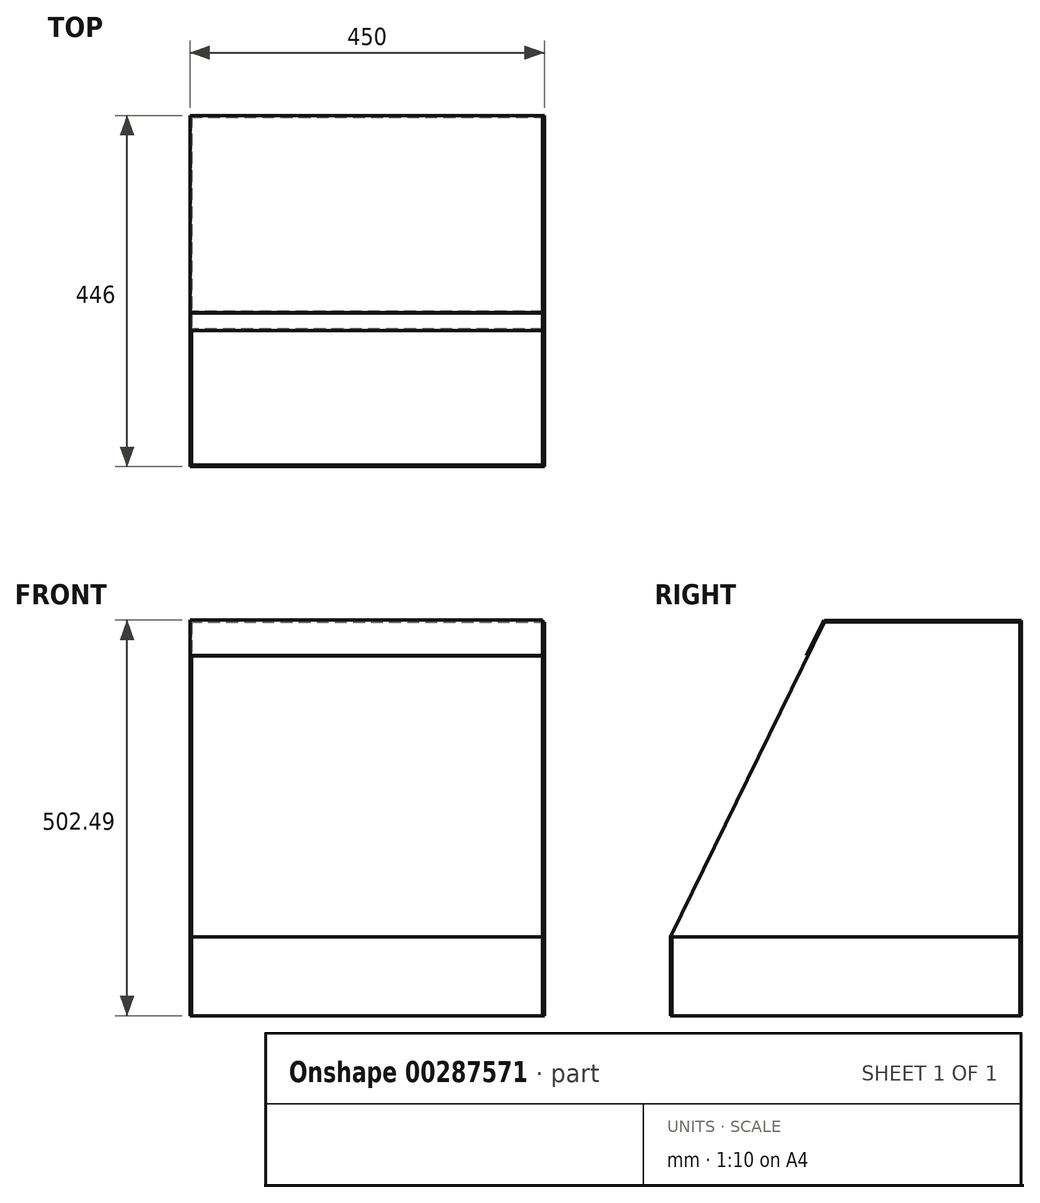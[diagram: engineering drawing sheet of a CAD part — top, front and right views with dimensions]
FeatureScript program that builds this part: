
annotation { "Feature Type Name" : "Feature", "Feature Type Description" : "" }
export const myFeature = defineFeature(function(context is Context, id is Id, definition is map)
    precondition{}
    {
        {
            var Q0;
            Q0=qCreatedBy(makeId("Top.planeOp"),FACE);
            var sketch = newSketch(context, id + "F0", { "sketchPlane" : qUnion([Q0])});
            skLineSegment(sketch, "E0.bottom", {"start": v(0, 448) * mm, "end": v(2, 448) * mm});
            skLineSegment(sketch, "E0.top", {"start": v(0, 2) * mm, "end": v(2, 2) * mm});
            skLineSegment(sketch, "E0.left", {"start": v(0, 448) * mm, "end": v(0, 2) * mm});
            skLineSegment(sketch, "E0.right", {"start": v(2, 448) * mm, "end": v(2, 2) * mm});
            skLineSegment(sketch, "E1.bottom", {"start": v(448, 448) * mm, "end": v(450, 448) * mm});
            skLineSegment(sketch, "E1.top", {"start": v(448, 2) * mm, "end": v(450, 2) * mm});
            skLineSegment(sketch, "E1.left", {"start": v(448, 448) * mm, "end": v(448, 2) * mm});
            skLineSegment(sketch, "E1.right", {"start": v(450, 448) * mm, "end": v(450, 2) * mm});
            skLineSegment(sketch, "E2.bottom", {"start": v(0, 450) * mm, "end": v(450, 450) * mm});
            skLineSegment(sketch, "E2.top", {"start": v(0, 448) * mm, "end": v(450, 448) * mm});
            skLineSegment(sketch, "E2.left", {"start": v(0, 450) * mm, "end": v(0, 448) * mm});
            skLineSegment(sketch, "E2.right", {"start": v(450, 450) * mm, "end": v(450, 448) * mm});
            skLineSegment(sketch, "E3.bottom", {"start": v(0, 2) * mm, "end": v(450, 2) * mm});
            skLineSegment(sketch, "E3.top", {"start": v(0, 0) * mm, "end": v(450, 0) * mm});
            skLineSegment(sketch, "E3.left", {"start": v(0, 2) * mm, "end": v(0, 0) * mm});
            skLineSegment(sketch, "E3.right", {"start": v(450, 2) * mm, "end": v(450, 0) * mm});
            skSolve(sketch);
        }
        {
            var Q0;
            Q0=sQuery(id+"F0.wireOp",EDGE,"E0.left");
            var Q1;
            Q1=sQuery(id+"F0.wireOp",EDGE,"E3.bottom");
            var Q2;
            Q2=sQuery(id+"F0.wireOp",EDGE,"E1.right");
            var Q3;
            Q3=sQuery(id+"F0.wireOp",EDGE,"E2.top");
            extrude(context, id + "F1", {"bodyType" : ToolBodyType.SURFACE, "surfaceEntities" : qUnion([Q0, Q1, Q2, Q3]), "depth" : 100 * mm});
        }
        {
            var Q0;
            Q0=makeQuery(id+"F1.opExtrude","SWEPT_FACE",FACE,{"disambiguationData":[OSD([sQuery(id+"F0.wireOp",EDGE,"E1.right")])]});
            var sketch = newSketch(context, id + "F2", { "sketchPlane" : qUnion([Q0])});
            skLineSegment(sketch, "E4", {"start": v(2, 100) * mm, "end": v(198, 500) * mm});
            skLineSegment(sketch, "E5", {"start": v(198, 500) * mm, "end": v(448, 500) * mm});
            skLineSegment(sketch, "E6", {"start": v(448, 500) * mm, "end": v(448, 100) * mm});
            skLineSegment(sketch, "E7", {"start": v(448, 100) * mm, "end": v(2, 100) * mm});
            skSolve(sketch);
        }
        {
            var Q0;
            Q0=makeQuery(id+"F2.imprint","IMPRINT",FACE,{"disambiguationData":[TD([[makeQuery(id+"F2.imprint","IMPRINT",EDGE,{"derivedFrom":sQuery(id+"F2.wireOp",EDGE,"E4")}),-1.0]])]});
            extrude(context, id + "F3", {"entities" : qUnion([Q0]), "oppositeDirection" : true, "depth" : 2 * mm});
        }
        {
            var Q0;
            Q0=makeQuery(id+"F1.opExtrude","SWEPT_FACE",FACE,{"disambiguationData":[OSD([sQuery(id+"F0.wireOp",EDGE,"E0.left")])]});
            var sketch = newSketch(context, id + "F4", { "sketchPlane" : qUnion([Q0])});
            skLineSegment(sketch, "E8", {"start": v(-2, 100) * mm, "end": v(-198, 500) * mm});
            skLineSegment(sketch, "E9", {"start": v(-198, 500) * mm, "end": v(-448, 500) * mm});
            skLineSegment(sketch, "E10", {"start": v(-448, 500) * mm, "end": v(-448, 100) * mm});
            skLineSegment(sketch, "E11", {"start": v(-448, 100) * mm, "end": v(-2, 100) * mm});
            skSolve(sketch);
        }
        {
            var Q0;
            Q0=makeQuery(id+"F4.imprint","IMPRINT",FACE,{"disambiguationData":[TD([[makeQuery(id+"F4.imprint","IMPRINT",EDGE,{"derivedFrom":sQuery(id+"F4.wireOp",EDGE,"E8")}),1.0]])]});
            extrude(context, id + "F5", {"entities" : qUnion([Q0]), "oppositeDirection" : true, "depth" : 2 * mm});
        }
        {
            var Q0;
            Q0=makeQuery(id+"F1.opExtrude","SWEPT_FACE",FACE,{"disambiguationData":[OSD([sQuery(id+"F0.wireOp",EDGE,"E2.top")])]});
            var sketch = newSketch(context, id + "F6", { "sketchPlane" : qUnion([Q0])});
            skLineSegment(sketch, "E12", {"start": v(-450, 100) * mm, "end": v(0, 100) * mm});
            skLineSegment(sketch, "E13", {"start": v(0, 100) * mm, "end": v(0, 500) * mm});
            skLineSegment(sketch, "E14", {"start": v(0, 500) * mm, "end": v(-450, 500) * mm});
            skLineSegment(sketch, "E15", {"start": v(-450, 500) * mm, "end": v(-450, 100) * mm});
            skSolve(sketch);
        }
        {
            var Q0;
            Q0=makeQuery(id+"F6.imprint","IMPRINT",FACE,{"disambiguationData":[TD([[makeQuery(id+"F6.imprint","IMPRINT",EDGE,{"derivedFrom":sQuery(id+"F6.wireOp",EDGE,"E12")}),1.0]])]});
            extrude(context, id + "F7", {"entities" : qUnion([Q0]), "oppositeDirection" : true, "depth" : 2 * mm});
        }
        {
            var Q0;
            Q0=makeQuery(id+"F3.opExtrude","SWEPT_FACE",FACE,{"disambiguationData":[OSD([sQuery(id+"F2.wireOp",EDGE,"E5")])]});
            var sketch = newSketch(context, id + "F8", { "sketchPlane" : qUnion([Q0])});
            skLineSegment(sketch, "E16.bottom", {"start": v(0, 448) * mm, "end": v(450, 448) * mm});
            skLineSegment(sketch, "E16.top", {"start": v(0, 198) * mm, "end": v(450, 198) * mm});
            skLineSegment(sketch, "E16.left", {"start": v(0, 448) * mm, "end": v(0, 198) * mm});
            skLineSegment(sketch, "E16.right", {"start": v(450, 448) * mm, "end": v(450, 198) * mm});
            skSolve(sketch);
        }
        {
            var Q0;
            {var subQ2=sQuery(id+"F8.wireOp",EDGE,"E16.left");Q0=makeQuery(id+"F8.imprint","IMPRINT",FACE,{"disambiguationData":[TD([[makeQuery(id+"F8.imprint","IMPRINT",EDGE,{"derivedFrom":subQ2}),1.0]])]});}
            extrude(context, id + "F9", {"entities" : qUnion([Q0]), "depth" : 2 * mm});
        }
        {
            var Q0;
            Q0=makeQuery(id+"F1.opExtrude","SWEPT_FACE",FACE,{"disambiguationData":[OSD([sQuery(id+"F0.wireOp",EDGE,"E2.top")])]});
            extrude(context, id + "F10", {"entities" : qUnion([Q0]), "oppositeDirection" : true, "depth" : 2 * mm});
        }
        {
            var Q0;
            Q0=makeQuery(id+"F1.opExtrude","SWEPT_FACE",FACE,{"disambiguationData":[OSD([sQuery(id+"F0.wireOp",EDGE,"E0.left")])]});
            extrude(context, id + "F11", {"entities" : qUnion([Q0]), "oppositeDirection" : true, "depth" : 2 * mm});
        }
        {
            var Q0;
            Q0=makeQuery(id+"F1.opExtrude","SWEPT_FACE",FACE,{"disambiguationData":[OSD([sQuery(id+"F0.wireOp",EDGE,"E3.bottom")])]});
            extrude(context, id + "F12", {"entities" : qUnion([Q0]), "oppositeDirection" : true, "depth" : 2 * mm});
        }
        {
            var Q0;
            Q0=makeQuery(id+"F1.opExtrude","SWEPT_FACE",FACE,{"disambiguationData":[OSD([sQuery(id+"F0.wireOp",EDGE,"E1.right")])]});
            extrude(context, id + "F13", {"entities" : qUnion([Q0]), "oppositeDirection" : true, "depth" : 2 * mm});
        }
        {
            var Q0;
            Q0=makeQuery(id+"F3.opExtrude","SWEPT_FACE",FACE,{"disambiguationData":[OSD([sQuery(id+"F2.wireOp",EDGE,"E4")])]});
            var sketch = newSketch(context, id + "F14", { "sketchPlane" : qUnion([Q0])});
            skLineSegment(sketch, "E17.bottom", {"start": v(448, 487.91) * mm, "end": v(0, 487.91) * mm});
            skLineSegment(sketch, "E17.top", {"start": v(448, 537.91) * mm, "end": v(0, 537.91) * mm});
            skLineSegment(sketch, "E17.left", {"start": v(448, 487.91) * mm, "end": v(448, 537.91) * mm});
            skLineSegment(sketch, "E17.right", {"start": v(0, 487.91) * mm, "end": v(0, 537.91) * mm});
            skSolve(sketch);
        }
        {
            var Q0;
            {var subQ3=sQuery(id+"F14.wireOp",EDGE,"E17.bottom");Q0=makeQuery(id+"F14.imprint","IMPRINT",FACE,{"disambiguationData":[TD([[makeQuery(id+"F14.imprint","IMPRINT",EDGE,{"derivedFrom":subQ3}),-1.0]])]});}
            extrude(context, id + "F15", {"entities" : qUnion([Q0]), "depth" : 2 * mm});
        }
    });
